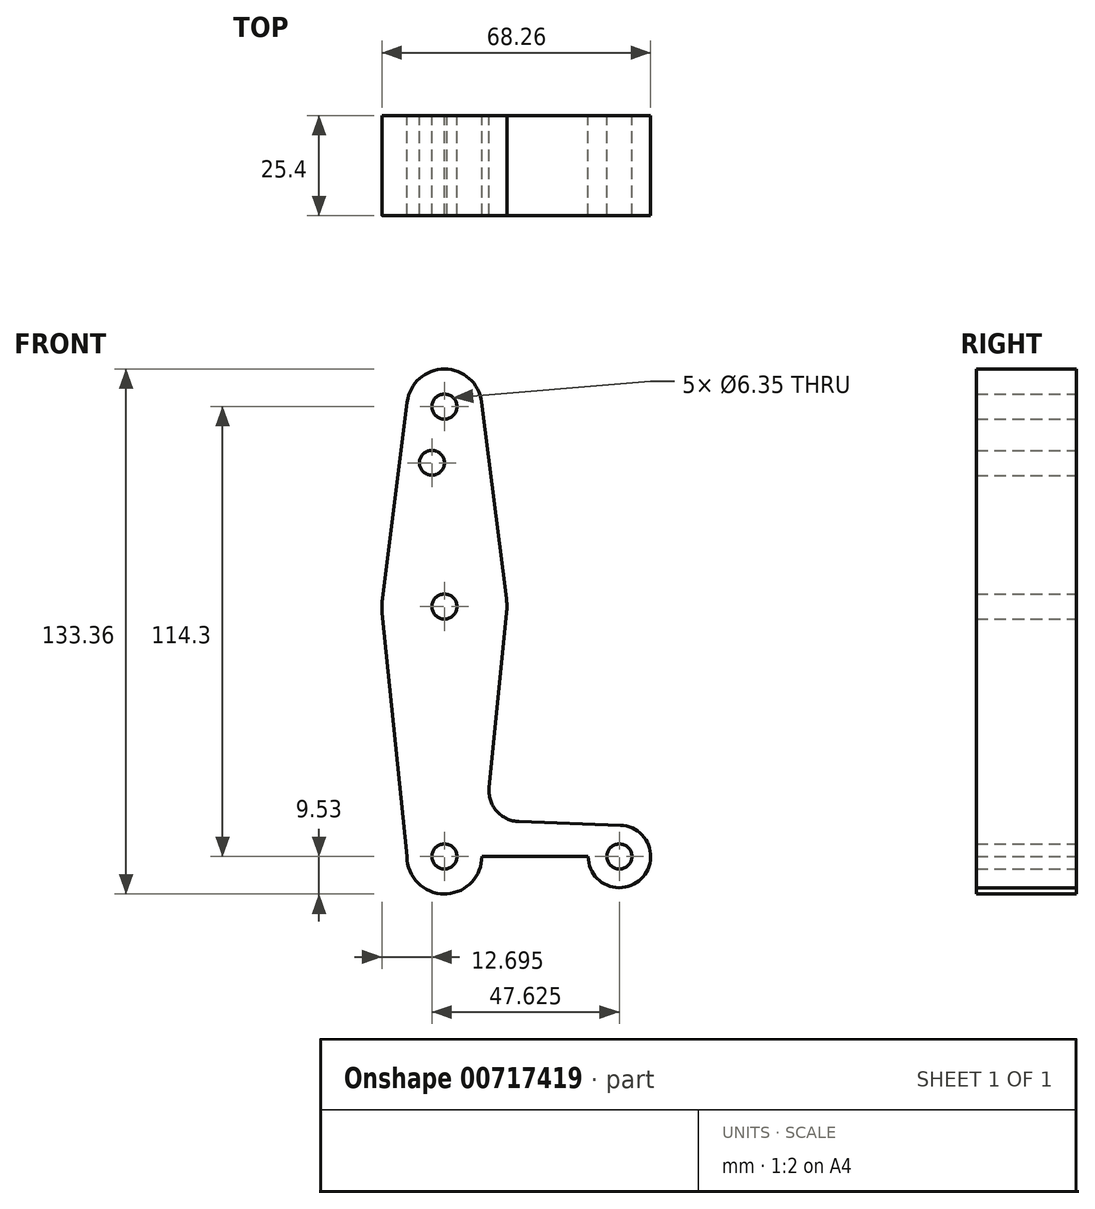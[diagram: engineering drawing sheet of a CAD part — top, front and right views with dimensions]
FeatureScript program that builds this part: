
annotation { "Feature Type Name" : "Feature", "Feature Type Description" : "" }
export const myFeature = defineFeature(function(context is Context, id is Id, definition is map)
    precondition{}
    {
        {
            var Q0;
            Q0=qCreatedBy(makeId("Front.planeOp"),FACE);
            var sketch = newSketch(context, id + "F0", { "sketchPlane" : qUnion([Q0])});
            skCircle(sketch, "E0", {"center": v(0, 0) * mm, "radius": 9.53 * mm});
            skLineSegment(sketch, "E1", {"start": v(0, 0) * mm, "end": v(0, 114.3) * mm});
            skLineSegment(sketch, "E2", {"start": v(44.45, 0) * mm, "end": v(0, 0) * mm});
            skCircle(sketch, "E3", {"center": v(44.45, 0) * mm, "radius": 7.94 * mm});
            skCircle(sketch, "E4", {"center": v(0, 114.3) * mm, "radius": 9.53 * mm});
            skCircle(sketch, "E5", {"center": v(0, 63.5) * mm, "radius": 15.88 * mm});
            skLineSegment(sketch, "E6", {"start": v(-9.45, 115.5) * mm, "end": v(-15.75, 65.48) * mm});
            skLineSegment(sketch, "E7", {"start": v(9.45, 115.5) * mm, "end": v(15.75, 65.48) * mm});
            skLineSegment(sketch, "E8", {"start": v(15.8, 61.91) * mm, "end": v(11.34, 17.59) * mm});
            skLineSegment(sketch, "E9", {"start": v(-9.53, 0) * mm, "end": v(-15.8, 61.9) * mm});
            skLineSegment(sketch, "E10", {"start": v(18.97, 8.85) * mm, "end": v(44.73, 7.93) * mm});
            skLineSegment(sketch, "E11", {"start": v(0, -9.53) * mm, "end": v(44.73, -7.93) * mm});
            skCircle(sketch, "E12", {"center": v(0, 114.3) * mm, "radius": 3.18 * mm});
            skCircle(sketch, "E13", {"center": v(0, 63.5) * mm, "radius": 3.18 * mm});
            skCircle(sketch, "E14", {"center": v(0, 0) * mm, "radius": 3.18 * mm});
            skCircle(sketch, "E15", {"center": v(44.45, 0) * mm, "radius": 3.18 * mm});
            skCircle(sketch, "E16", {"center": v(-3.18, 100.03) * mm, "radius": 3.18 * mm});
            skArc(sketch, "E17.filletArc", {"start": v(11.34, 17.59) * mm, "mid": v(13.26, 11.57) * mm, "end": v(18.97, 8.85) * mm});
            skSolve(sketch);
        }
        {
            var Q0;
            {var subQ0=sQuery(id+"F0.wireOp",EDGE,"E11");var subQ1=sQuery(id+"F0.wireOp",EDGE,"E0");var subQ2=makeQuery(id+"F0.imprint","INTERSECT",VERTEX,{"disambiguationData":[OD(0.0)],"derivedFrom":[subQ1,subQ0]});Q0=makeQuery(id+"F0.imprint","IMPRINT",FACE,{"disambiguationData":[TD([[makeQuery(id+"F0.imprint","IMPRINT",EDGE,{"disambiguationData":[TD([[subQ2,-1.0]])],"derivedFrom":subQ1}),1.0]])]});}
            var Q1;
            {var subQ0=sQuery(id+"F0.wireOp",EDGE,"E9");Q1=makeQuery(id+"F0.imprint","IMPRINT",FACE,{"disambiguationData":[TD([[makeQuery(id+"F0.imprint","IMPRINT",EDGE,{"derivedFrom":subQ0}),-1.0]])]});}
            var Q2;
            {var subQ0=sQuery(id+"F0.wireOp",EDGE,"E11");var subQ1=sQuery(id+"F0.wireOp",EDGE,"E0");var subQ2=makeQuery(id+"F0.imprint","INTERSECT",VERTEX,{"disambiguationData":[OD(1.0)],"derivedFrom":[subQ1,subQ0]});Q2=makeQuery(id+"F0.imprint","IMPRINT",FACE,{"disambiguationData":[TD([[makeQuery(id+"F0.imprint","IMPRINT",EDGE,{"disambiguationData":[TD([[subQ2,-1.0]])],"derivedFrom":subQ1}),-1.0]])]});}
            var Q3;
            {var subQ5=sQuery(id+"F0.wireOp",EDGE,"E7");Q3=makeQuery(id+"F0.imprint","IMPRINT",FACE,{"disambiguationData":[TD([[makeQuery(id+"F0.imprint","IMPRINT",EDGE,{"derivedFrom":subQ5}),-1.0]])]});}
            var Q4;
            Q4=makeQuery(id+"F0.imprint","IMPRINT",FACE,{"disambiguationData":[TD([[makeQuery(id+"F0.imprint","IMPRINT",EDGE,{"derivedFrom":sQuery(id+"F0.wireOp",EDGE,"E15")}),-1.0]])]});
            var Q5;
            Q5=makeQuery(id+"F0.imprint","IMPRINT",FACE,{"disambiguationData":[TD([[makeQuery(id+"F0.imprint","IMPRINT",EDGE,{"derivedFrom":sQuery(id+"F0.wireOp",EDGE,"E12")}),-1.0]])]});
            var Q6;
            {var subQ0=sQuery(id+"F0.wireOp",EDGE,"E5");var subQ2=sQuery(id+"F0.wireOp",EDGE,"E1");var subQ7=makeQuery(id+"F0.imprint","INTERSECT",VERTEX,{"disambiguationData":[OD(0.0)],"derivedFrom":[subQ2,subQ0]});Q6=makeQuery(id+"F0.imprint","IMPRINT",FACE,{"disambiguationData":[TD([[makeQuery(id+"F0.imprint","IMPRINT",EDGE,{"disambiguationData":[TD([[subQ7,-1.0]])],"derivedFrom":subQ2}),-1.0]])]});}
            var Q7;
            {var subQ0=sQuery(id+"F0.wireOp",EDGE,"E5");var subQ2=sQuery(id+"F0.wireOp",EDGE,"E1");var subQ7=makeQuery(id+"F0.imprint","INTERSECT",VERTEX,{"disambiguationData":[OD(0.0)],"derivedFrom":[subQ2,subQ0]});Q7=makeQuery(id+"F0.imprint","IMPRINT",FACE,{"disambiguationData":[TD([[makeQuery(id+"F0.imprint","IMPRINT",EDGE,{"disambiguationData":[TD([[subQ7,-1.0]])],"derivedFrom":subQ2}),1.0]])]});}
            var Q8;
            {var subQ9=sQuery(id+"F0.wireOp",EDGE,"E8");Q8=makeQuery(id+"F0.imprint","IMPRINT",FACE,{"disambiguationData":[TD([[makeQuery(id+"F0.imprint","IMPRINT",EDGE,{"derivedFrom":subQ9}),-1.0]])]});}
            var Q9;
            {var subQ1=sQuery(id+"F0.wireOp",EDGE,"E0");var subQ5=makeQuery(id+"F0.imprint","INTERSECT",VERTEX,{"derivedFrom":[subQ1,sQuery(id+"F0.wireOp",EDGE,"E9")]});Q9=makeQuery(id+"F0.imprint","IMPRINT",FACE,{"disambiguationData":[TD([[makeQuery(id+"F0.imprint","IMPRINT",EDGE,{"disambiguationData":[TD([[subQ5,1.0]])],"derivedFrom":subQ1}),1.0]])]});}
            var Q10;
            {var subQ0=sQuery(id+"F0.wireOp",EDGE,"E1");var subQ1=sQuery(id+"F0.wireOp",EDGE,"E0");var subQ2=makeQuery(id+"F0.imprint","INTERSECT",VERTEX,{"derivedFrom":[subQ1,subQ0]});Q10=makeQuery(id+"F0.imprint","IMPRINT",FACE,{"disambiguationData":[TD([[makeQuery(id+"F0.imprint","IMPRINT",EDGE,{"disambiguationData":[TD([[subQ2,1.0]])],"derivedFrom":subQ1}),1.0]])]});}
            var Q11;
            {var subQ0=sQuery(id+"F0.wireOp",EDGE,"E6");Q11=makeQuery(id+"F0.imprint","IMPRINT",FACE,{"disambiguationData":[TD([[makeQuery(id+"F0.imprint","IMPRINT",EDGE,{"derivedFrom":subQ0}),1.0]])]});}
            extrude(context, id + "F1", {"entities" : qUnion([Q0, Q1, Q2, Q3, Q4, Q5, Q6, Q7, Q8, Q9, Q10, Q11]), "depth" : 25.4 * mm, "offsetDistance" : 25.4 * mm});
        }
    });
